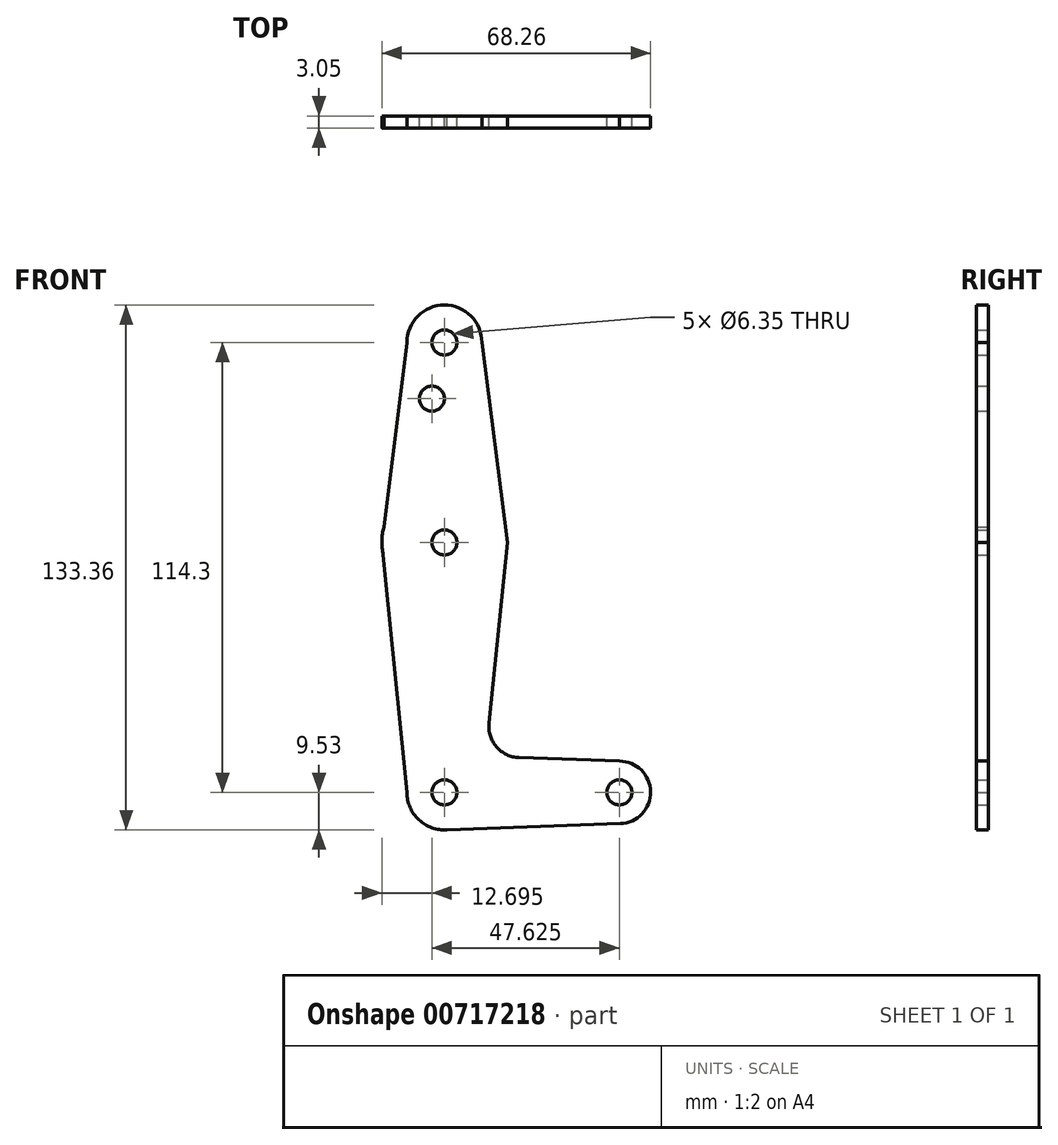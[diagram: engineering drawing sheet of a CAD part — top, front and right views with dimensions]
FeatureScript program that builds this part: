
annotation { "Feature Type Name" : "Feature", "Feature Type Description" : "" }
export const myFeature = defineFeature(function(context is Context, id is Id, definition is map)
    precondition{}
    {
        {
            var Q0;
            Q0=qCreatedBy(makeId("Front.planeOp"),FACE);
            var sketch = newSketch(context, id + "F0", { "sketchPlane" : qUnion([Q0])});
            skCircle(sketch, "E0", {"center": v(0, 0) * mm, "radius": 9.53 * mm});
            skCircle(sketch, "E1", {"center": v(0, 114.3) * mm, "radius": 9.53 * mm});
            skCircle(sketch, "E2", {"center": v(44.45, 0) * mm, "radius": 7.94 * mm});
            skCircle(sketch, "E3", {"center": v(0, 63.5) * mm, "radius": 15.88 * mm});
            skLineSegment(sketch, "E4", {"start": v(9.52, 114.3) * mm, "end": v(16, 63.5) * mm});
            skLineSegment(sketch, "E5", {"start": v(16, 63.5) * mm, "end": v(11.32, 17.6) * mm});
            skLineSegment(sketch, "E6", {"start": v(-9.53, 114.3) * mm, "end": v(-15.88, 63.5) * mm});
            skLineSegment(sketch, "E7", {"start": v(-15.88, 63.5) * mm, "end": v(-9.52, 0) * mm});
            skLineSegment(sketch, "E8", {"start": v(44.45, 7.94) * mm, "end": v(18.95, 8.85) * mm});
            skLineSegment(sketch, "E9", {"start": v(0, -9.53) * mm, "end": v(44.73, -7.93) * mm});
            skCircle(sketch, "E10", {"center": v(0, 114.3) * mm, "radius": 3.18 * mm});
            skCircle(sketch, "E11", {"center": v(0, 63.5) * mm, "radius": 3.17 * mm});
            skCircle(sketch, "E12", {"center": v(0, 0) * mm, "radius": 3.18 * mm});
            skCircle(sketch, "E13", {"center": v(44.45, 0) * mm, "radius": 3.18 * mm});
            skCircle(sketch, "E14", {"center": v(-3.18, 100.03) * mm, "radius": 3.18 * mm});
            skArc(sketch, "E15.filletArc", {"start": v(11.32, 17.6) * mm, "mid": v(13.24, 11.57) * mm, "end": v(18.95, 8.85) * mm});
            skSolve(sketch);
        }
        {
            var Q0;
            Q0 = qSketchRegion(id + "F0", true);
            extrude(context, id + "F1", {"entities" : qUnion([Q0]), "depth" : 3.05 * mm, "offsetDistance" : 25.4 * mm});
        }
    });
